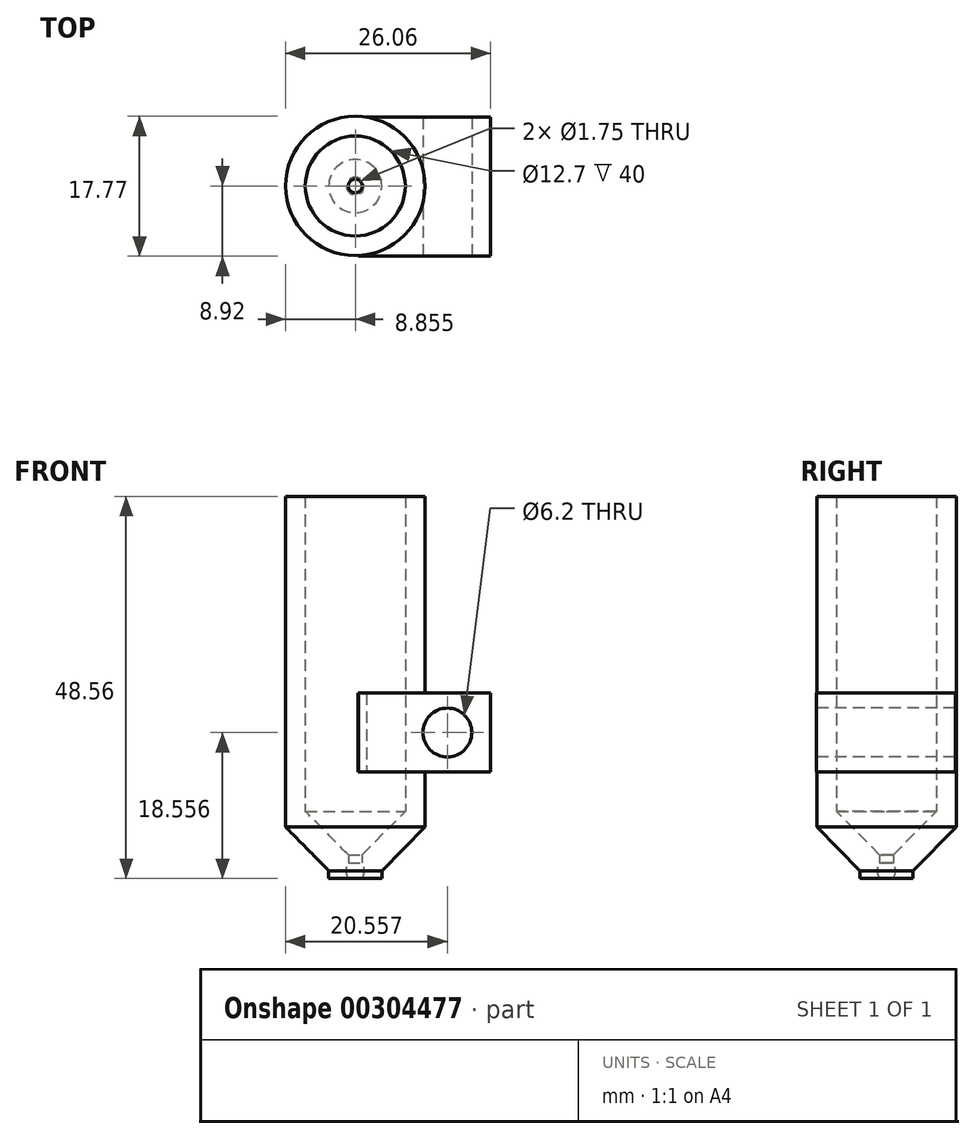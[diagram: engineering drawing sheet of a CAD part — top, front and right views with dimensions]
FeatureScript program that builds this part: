
annotation { "Feature Type Name" : "Feature", "Feature Type Description" : "" }
export const myFeature = defineFeature(function(context is Context, id is Id, definition is map)
    precondition{}
    {
        {
            var Q0;
            Q0=qCreatedBy(makeId("Front.planeOp"),FACE);
            var sketch = newSketch(context, id + "F0", { "sketchPlane" : qUnion([Q0])});
            skCircle(sketch, "E0", {"center": v(0, 0) * mm, "radius": 0.88 * mm});
            skCircle(sketch, "E1", {"center": v(0, 0) * mm, "radius": 2 * mm});
            skSolve(sketch);
        }
        {
            var Q0;
            Q0=makeQuery(id+"F0.imprint","IMPRINT",FACE,{"disambiguationData":[TD([[makeQuery(id+"F0.imprint","IMPRINT",EDGE,{"derivedFrom":sQuery(id+"F0.wireOp",EDGE,"E0")}),-1.0]])]});
            var sketch = newSketch(context, id + "F1", { "sketchPlane" : qUnion([Q0])});
            skLineSegment(sketch, "E2", {"start": v(-0.88, 0) * mm, "end": v(-1.75, 0) * mm});
            skLineSegment(sketch, "E3", {"start": v(-1.75, 0) * mm, "end": v(-1.75, 2) * mm});
            skLineSegment(sketch, "E4", {"start": v(-1.75, 2) * mm, "end": v(-1.75, 6) * mm});
            skLineSegment(sketch, "E5", {"start": v(-0.88, 0) * mm, "end": v(-0.88, 6) * mm});
            skLineSegment(sketch, "E6", {"start": v(-7.22, 7.56) * mm, "end": v(-1.75, 2) * mm});
            skLineSegment(sketch, "E7", {"start": v(-9.72, 5.56) * mm, "end": v(-4.25, 0) * mm});
            skLineSegment(sketch, "E8", {"start": v(-4.25, 0) * mm, "end": v(-4.25, -1) * mm});
            skLineSegment(sketch, "E9", {"start": v(-4.25, -1) * mm, "end": v(-1.75, -1) * mm});
            skLineSegment(sketch, "E10", {"start": v(-1.75, -1) * mm, "end": v(-1.75, 0) * mm});
            skPoint(sketch, "E11.orphan", {"position": v(0, 0) * mm});
            skLineSegment(sketch, "E12", {"start": v(-7.23, 23.8) * mm, "end": v(-7.23, 7.56) * mm});
            skLineSegment(sketch, "E13", {"start": v(-7.23, 7.56) * mm, "end": v(-9.72, 7.56) * mm});
            skLineSegment(sketch, "E14", {"start": v(-9.72, 7.56) * mm, "end": v(-9.72, 47.56) * mm});
            skLineSegment(sketch, "E15", {"start": v(-9.72, 47.56) * mm, "end": v(-7.22, 47.56) * mm});
            skLineSegment(sketch, "E16", {"start": v(-7.22, 47.56) * mm, "end": v(-7.23, 23.8) * mm});
            skPoint(sketch, "E17.end.orphan", {"position": v(-13.58, 54) * mm});
            skLineSegment(sketch, "E18", {"start": v(-9.72, 7.56) * mm, "end": v(-9.72, 5.56) * mm});
            skPoint(sketch, "E19.start.orphan", {"position": v(-13.58, 14) * mm});
            skSolve(sketch);
        }
        {
            var Q0;
            Q0=makeQuery(id+"F1.imprint","IMPRINT",FACE,{"disambiguationData":[TD([[makeQuery(id+"F1.imprint","IMPRINT",EDGE,{"derivedFrom":sQuery(id+"F1.wireOp",EDGE,"E12")}),-1.0]])]});
            var Q1;
            {var subQ5=sQuery(id+"F1.wireOp",EDGE,"E6");Q1=makeQuery(id+"F1.imprint","IMPRINT",FACE,{"disambiguationData":[TD([[makeQuery(id+"F1.imprint","IMPRINT",EDGE,{"derivedFrom":subQ5}),-1.0]])]});}
            var Q2;
            Q2=sQuery(id+"F1.wireOp",EDGE,"E5");
            revolve(context, id + "F2", {"entities" : qUnion([Q0, Q1]), "axis" : qUnion([Q2]), "revolveType" : RevolveType.FULL});
        }
        {
            var Q0;
            Q0=makeQuery(id+"F2.opRevolve","SWEPT_FACE",FACE,{"disambiguationData":[OSD([sQuery(id+"F1.wireOp",EDGE,"E15")])]});
            var sketch = newSketch(context, id + "F3", { "sketchPlane" : qUnion([Q0])});
            skLineSegment(sketch, "E20", {"start": v(0, 8.8) * mm, "end": v(16.97, 8.8) * mm});
            skCircle(sketch, "E21", {"center": v(-0.88, 0) * mm, "radius": 8.84 * mm});
            skLineSegment(sketch, "E22", {"start": v(7.97, 0) * mm, "end": v(7.97, -13.16) * mm});
            skLineSegment(sketch, "E23", {"start": v(-0.84, -8.85) * mm, "end": v(11.97, -8.85) * mm});
            skLineSegment(sketch, "E24", {"start": v(7.97, -8.85) * mm, "end": v(16.97, -8.85) * mm});
            skPoint(sketch, "E24.endSnap0", {"position": v(14.7, -8.85) * mm});
            skLineSegment(sketch, "E25", {"start": v(16.97, -8.85) * mm, "end": v(16.97, 0) * mm});
            skLineSegment(sketch, "E26", {"start": v(16.97, 0) * mm, "end": v(16.97, 8.8) * mm});
            skSolve(sketch);
        }
        {
            var Q0;
            {var subQ6=sQuery(id+"F3.wireOp",EDGE,"E20");Q0=makeQuery(id+"F3.imprint","IMPRINT",FACE,{"disambiguationData":[TD([[makeQuery(id+"F3.imprint","IMPRINT",EDGE,{"derivedFrom":subQ6}),-1.0]])]});}
            cPlane(context, id + "F4", {"entities" : qUnion([Q0]), "cplaneType" : CPlaneType.OFFSET, "offset" : 25 * mm, "oppositeDirection" : true, "width" : 150 * mm, "height" : 150 * mm});
        }
        {
            var Q0;
            Q0=qCreatedBy(id+"F4.planeOp",FACE);
            var sketch = newSketch(context, id + "F5", { "sketchPlane" : qUnion([Q0])});
            skLineSegment(sketch, "E27", {"start": v(0.35, 8.73) * mm, "end": v(16.33, 8.73) * mm});
            skLineSegment(sketch, "E28", {"start": v(8.33, -0.07) * mm, "end": v(8.33, -13.23) * mm});
            skLineSegment(sketch, "E29", {"start": v(-0.49, -8.92) * mm, "end": v(12.32, -8.92) * mm});
            skLineSegment(sketch, "E30", {"start": v(8.33, -8.92) * mm, "end": v(16.33, -8.92) * mm});
            skPoint(sketch, "E30.endSnap0", {"position": v(14.05, -8.92) * mm});
            skLineSegment(sketch, "E31", {"start": v(16.33, -8.92) * mm, "end": v(16.33, -0.07) * mm});
            skLineSegment(sketch, "E32", {"start": v(16.33, -0.07) * mm, "end": v(16.33, 8.73) * mm});
            skLineSegment(sketch, "E33", {"start": v(0.35, 8.73) * mm, "end": v(5.18, 5.59) * mm});
            skLineSegment(sketch, "E34", {"start": v(5.18, 5.59) * mm, "end": v(6.88, -0.89) * mm});
            skLineSegment(sketch, "E35", {"start": v(6.88, -0.89) * mm, "end": v(5.22, -4.38) * mm});
            skLineSegment(sketch, "E36", {"start": v(5.22, -4.38) * mm, "end": v(1.4, -7.4) * mm});
            skLineSegment(sketch, "E37", {"start": v(1.4, -7.4) * mm, "end": v(-0.92, -8.17) * mm});
            skLineSegment(sketch, "E38", {"start": v(-0.92, -8.17) * mm, "end": v(-0.49, -8.92) * mm});
            skSolve(sketch);
        }
        {
            var Q0;
            Q0=makeQuery(id+"F5.imprint","IMPRINT",FACE,{"disambiguationData":[TD([[makeQuery(id+"F5.imprint","IMPRINT",EDGE,{"derivedFrom":sQuery(id+"F5.wireOp",EDGE,"E27")}),-1.0]])]});
            extrude(context, id + "F6", {"entities" : qUnion([Q0]), "operationType" : NewBodyOperationType.ADD, "oppositeDirection" : true, "depth" : 10 * mm});
        }
        {
            var Q0;
            Q0=makeQuery(id+"F6.opExtrude","SWEPT_FACE",FACE,{"disambiguationData":[OSD([sQuery(id+"F5.wireOp",EDGE,"E29"),sQuery(id+"F5.wireOp",EDGE,"E30")])]});
            var sketch = newSketch(context, id + "F7", { "sketchPlane" : qUnion([Q0])});
            skLineSegment(sketch, "E39", {"start": v(16.33, 17.56) * mm, "end": v(11.33, 17.56) * mm});
            skLineSegment(sketch, "E40", {"start": v(11.33, 17.56) * mm, "end": v(10.83, 17.56) * mm});
            skCircle(sketch, "E41", {"center": v(10.83, 17.56) * mm, "radius": 3.1 * mm});
            skSolve(sketch);
        }
        {
            var Q0;
            Q0=makeQuery(id+"F7.imprint","IMPRINT",FACE,{"disambiguationData":[TD([[makeQuery(id+"F7.imprint","IMPRINT",EDGE,{"derivedFrom":sQuery(id+"F7.wireOp",EDGE,"E41")}),1.0]])]});
            extrude(context, id + "F8", {"entities" : qUnion([Q0]), "operationType" : NewBodyOperationType.REMOVE, "oppositeDirection" : true, "depth" : 25 * mm});
        }
    });
